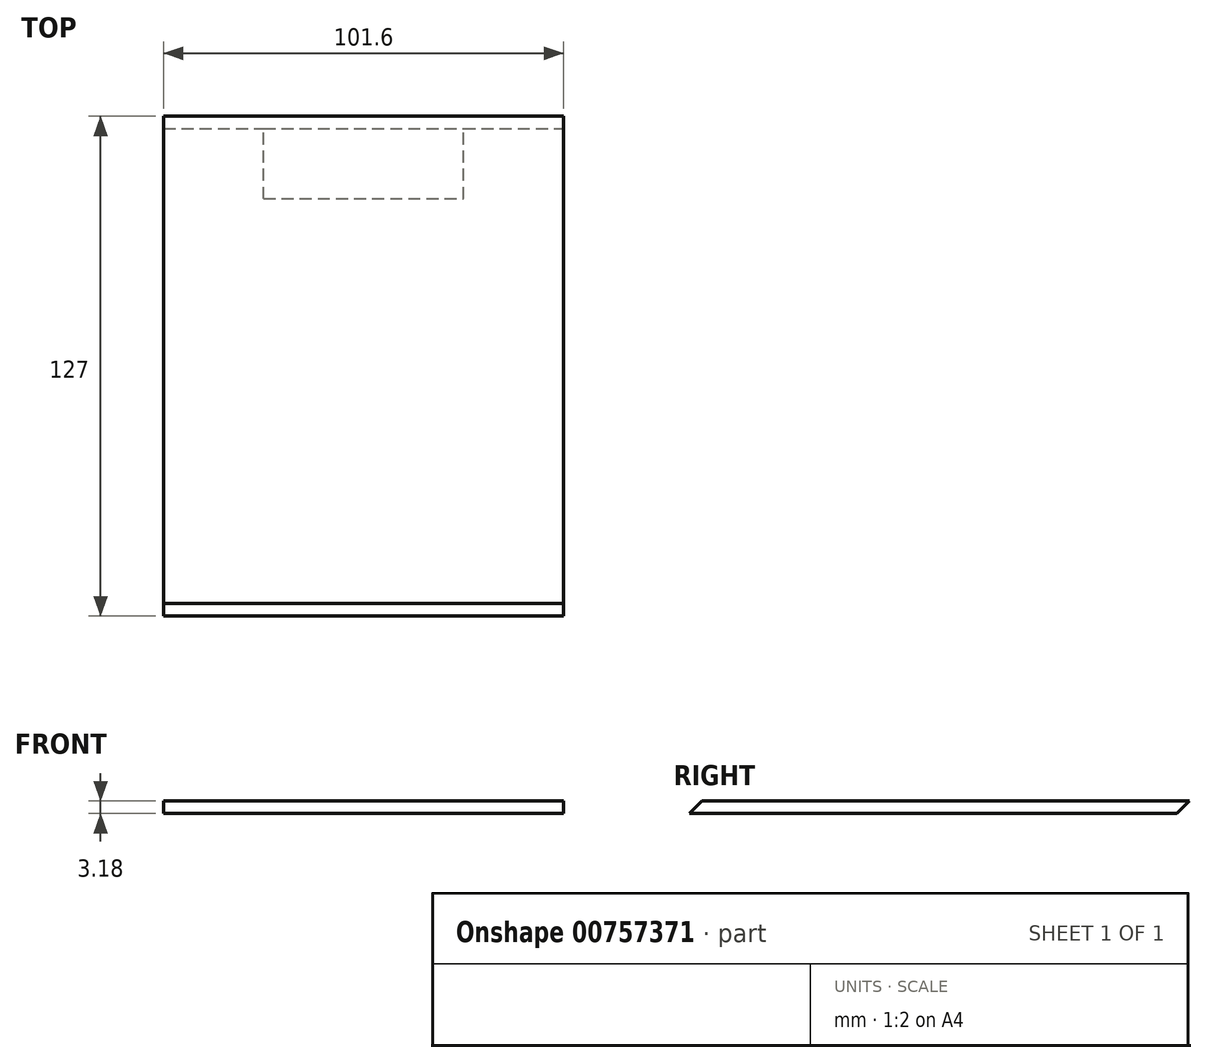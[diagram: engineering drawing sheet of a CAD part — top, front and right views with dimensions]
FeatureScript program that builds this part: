
annotation { "Feature Type Name" : "Feature", "Feature Type Description" : "" }
export const myFeature = defineFeature(function(context is Context, id is Id, definition is map)
    precondition{}
    {
        {
            var Q0;
            Q0=qCreatedBy(makeId("Top.planeOp"),FACE);
            var sketch = newSketch(context, id + "F0", { "sketchPlane" : qUnion([Q0])});
            skLineSegment(sketch, "E0.bottom", {"start": v(-45.54, 74.34) * mm, "end": v(56.06, 74.34) * mm});
            skLineSegment(sketch, "E0.top", {"start": v(-45.54, -52.66) * mm, "end": v(56.06, -52.66) * mm});
            skLineSegment(sketch, "E0.left", {"start": v(-45.54, 74.34) * mm, "end": v(-45.54, -52.66) * mm});
            skLineSegment(sketch, "E0.right", {"start": v(56.06, 74.34) * mm, "end": v(56.06, -52.66) * mm});
            skSolve(sketch);
        }
        {
            var Q0;
            Q0 = qSketchRegion(id + "F0", true);
            var Q1;
            Q1=makeQuery(id+"F0.imprint","IMPRINT",FACE,{"disambiguationData":[TD([[makeQuery(id+"F0.imprint","IMPRINT",EDGE,{"derivedFrom":sQuery(id+"F0.wireOp",EDGE,"E0.bottom")}),-1.0]])]});
            extrude(context, id + "F1", {"entities" : qUnion([Q0, Q1]), "depth" : 3.17 * mm, "offsetDistance" : 25.4 * mm});
        }
        {
            var Q0;
            Q0=makeQuery(id+"F1.opExtrude","CAP_EDGE",EDGE,{"disambiguationData":[OSD([sQuery(id+"F0.wireOp",EDGE,"E0.bottom")])],"isStart":true});
            chamfer(context, id + "F2", {"entities" : qUnion([Q0]), "width" : 3.17 * mm, "tangentPropagation" : true});
        }
        {
            var Q0;
            Q0=makeQuery(id+"F1.opExtrude","CAP_EDGE",EDGE,{"disambiguationData":[OSD([sQuery(id+"F0.wireOp",EDGE,"E0.top")])],"isStart":false});
            chamfer(context, id + "F3", {"entities" : qUnion([Q0]), "width" : 3.17 * mm, "tangentPropagation" : true});
        }
        {
            var Q0;
            Q0=makeQuery(id+"F1.opExtrude","CAP_FACE",FACE,{"disambiguationData":[OSD([sQuery(id+"F0.wireOp",EDGE,"E0.bottom"),sQuery(id+"F0.wireOp",EDGE,"E0.top"),sQuery(id+"F0.wireOp",EDGE,"E0.left"),sQuery(id+"F0.wireOp",EDGE,"E0.right")])],"isStart":true});
            var sketch = newSketch(context, id + "F4", { "sketchPlane" : qUnion([Q0])});
            skLineSegment(sketch, "E1.bottom", {"start": v(-26.5, -71.16) * mm, "end": v(11.6, -71.16) * mm});
            skLineSegment(sketch, "E1.top", {"start": v(-26.5, -53.4) * mm, "end": v(11.6, -53.4) * mm});
            skLineSegment(sketch, "E1.right", {"start": v(11.6, -71.16) * mm, "end": v(11.6, -53.4) * mm});
            skLineSegment(sketch, "E2", {"start": v(-26.5, -53.4) * mm, "end": v(-20.14, -53.4) * mm});
            skLineSegment(sketch, "E3.bottom", {"start": v(-20.14, -53.4) * mm, "end": v(30.66, -53.4) * mm});
            skLineSegment(sketch, "E3.top", {"start": v(-20.14, -71.16) * mm, "end": v(30.66, -71.16) * mm});
            skLineSegment(sketch, "E3.left", {"start": v(-20.14, -53.4) * mm, "end": v(-20.14, -71.16) * mm});
            skLineSegment(sketch, "E3.right", {"start": v(30.66, -53.4) * mm, "end": v(30.66, -71.16) * mm});
            skSolve(sketch);
        }
        {
            var Q0;
            Q0 = qSketchRegion(id + "F4", true);
            extrude(context, id + "F5", {"entities" : qUnion([Q0]), "operationType" : NewBodyOperationType.REMOVE, "oppositeDirection" : true, "depth" : 1 / 203.2 * mm, "offsetDistance" : 25.4 * mm});
        }
    });
